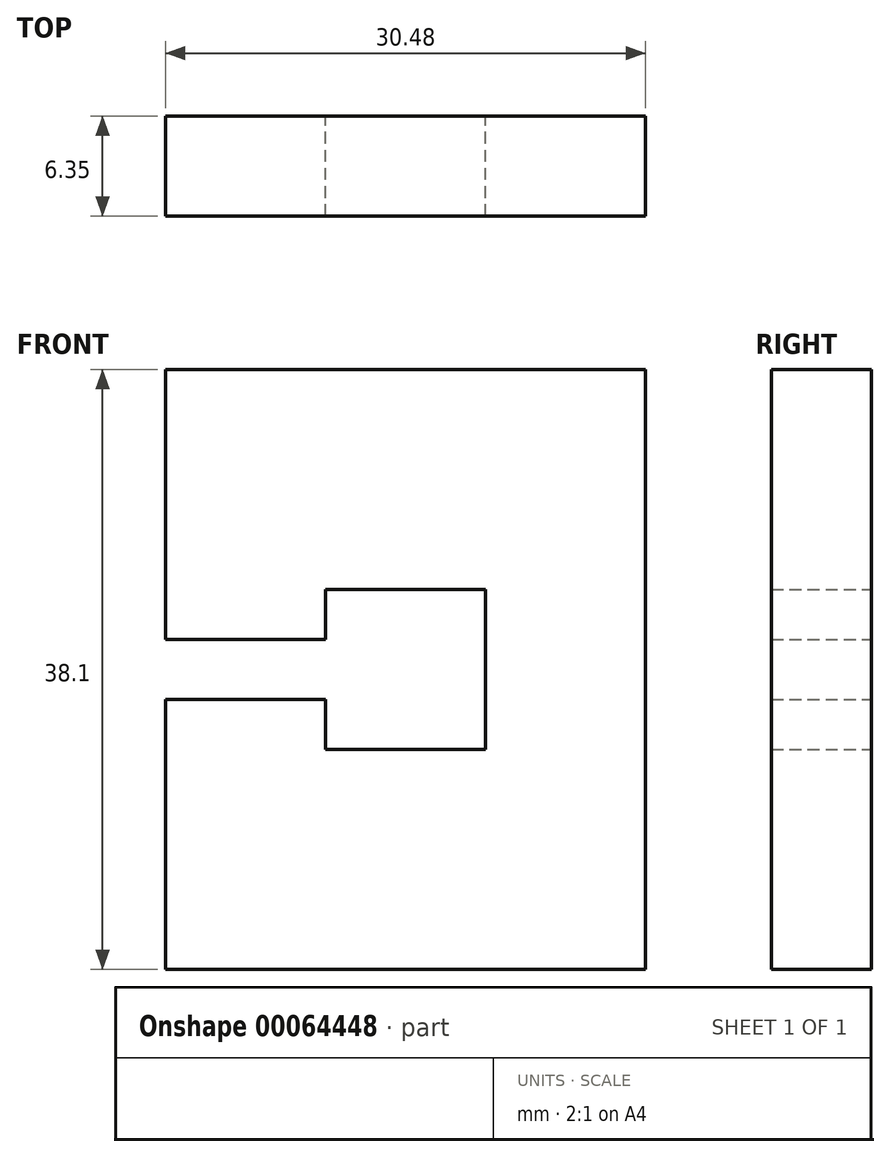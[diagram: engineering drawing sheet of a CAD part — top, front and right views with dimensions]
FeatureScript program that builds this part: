
annotation { "Feature Type Name" : "Feature", "Feature Type Description" : "" }
export const myFeature = defineFeature(function(context is Context, id is Id, definition is map)
    precondition{}
    {
        {
            var Q0;
            Q0=qCreatedBy(makeId("Front.planeOp"),FACE);
            var sketch = newSketch(context, id + "F0", { "sketchPlane" : qUnion([Q0])});
            skLineSegment(sketch, "E0.rect.bottom", {"start": v(15.24, 19.05) * mm, "end": v(-15.24, 19.05) * mm});
            skLineSegment(sketch, "E0.rect.top", {"start": v(15.24, -19.05) * mm, "end": v(-15.24, -19.05) * mm});
            skLineSegment(sketch, "E0.rect.left", {"start": v(15.24, 19.05) * mm, "end": v(15.24, -19.05) * mm});
            skLineSegment(sketch, "E0.rect.right", {"start": v(-15.24, 19.05) * mm, "end": v(-15.24, 1.9) * mm});
            skPoint(sketch, "E0.rect.middle", {"position": v(0, 0) * mm});
            skLineSegment(sketch, "E1.rect.bottom", {"start": v(5.08, 5.08) * mm, "end": v(-5.08, 5.08) * mm});
            skLineSegment(sketch, "E1.rect.top", {"start": v(5.08, -5.08) * mm, "end": v(-5.08, -5.08) * mm});
            skLineSegment(sketch, "E1.rect.left", {"start": v(5.08, 5.08) * mm, "end": v(5.08, -5.08) * mm});
            skLineSegment(sketch, "E1.rect.right", {"start": v(-5.08, 5.08) * mm, "end": v(-5.08, 1.9) * mm});
            skLineSegment(sketch, "E2.bottom", {"start": v(-15.24, 1.9) * mm, "end": v(-5.08, 1.9) * mm});
            skLineSegment(sketch, "E2.top", {"start": v(-15.24, -1.9) * mm, "end": v(-5.08, -1.9) * mm});
            skLineSegment(sketch, "E2.right", {"start": v(15.24, 1.9) * mm, "end": v(15.24, -1.9) * mm});
            skLineSegment(sketch, "E3.trimOffspring", {"start": v(-5.08, -1.9) * mm, "end": v(-5.08, -5.08) * mm});
            skLineSegment(sketch, "E4.trimOffspring", {"start": v(-15.24, -1.9) * mm, "end": v(-15.24, -19.05) * mm});
            skSolve(sketch);
        }
        {
            var Q0;
            Q0 = qSketchRegion(id + "F0", true);
            extrude(context, id + "F1", {"entities" : qUnion([Q0]), "depth" : 6.35 * mm});
        }
    });
